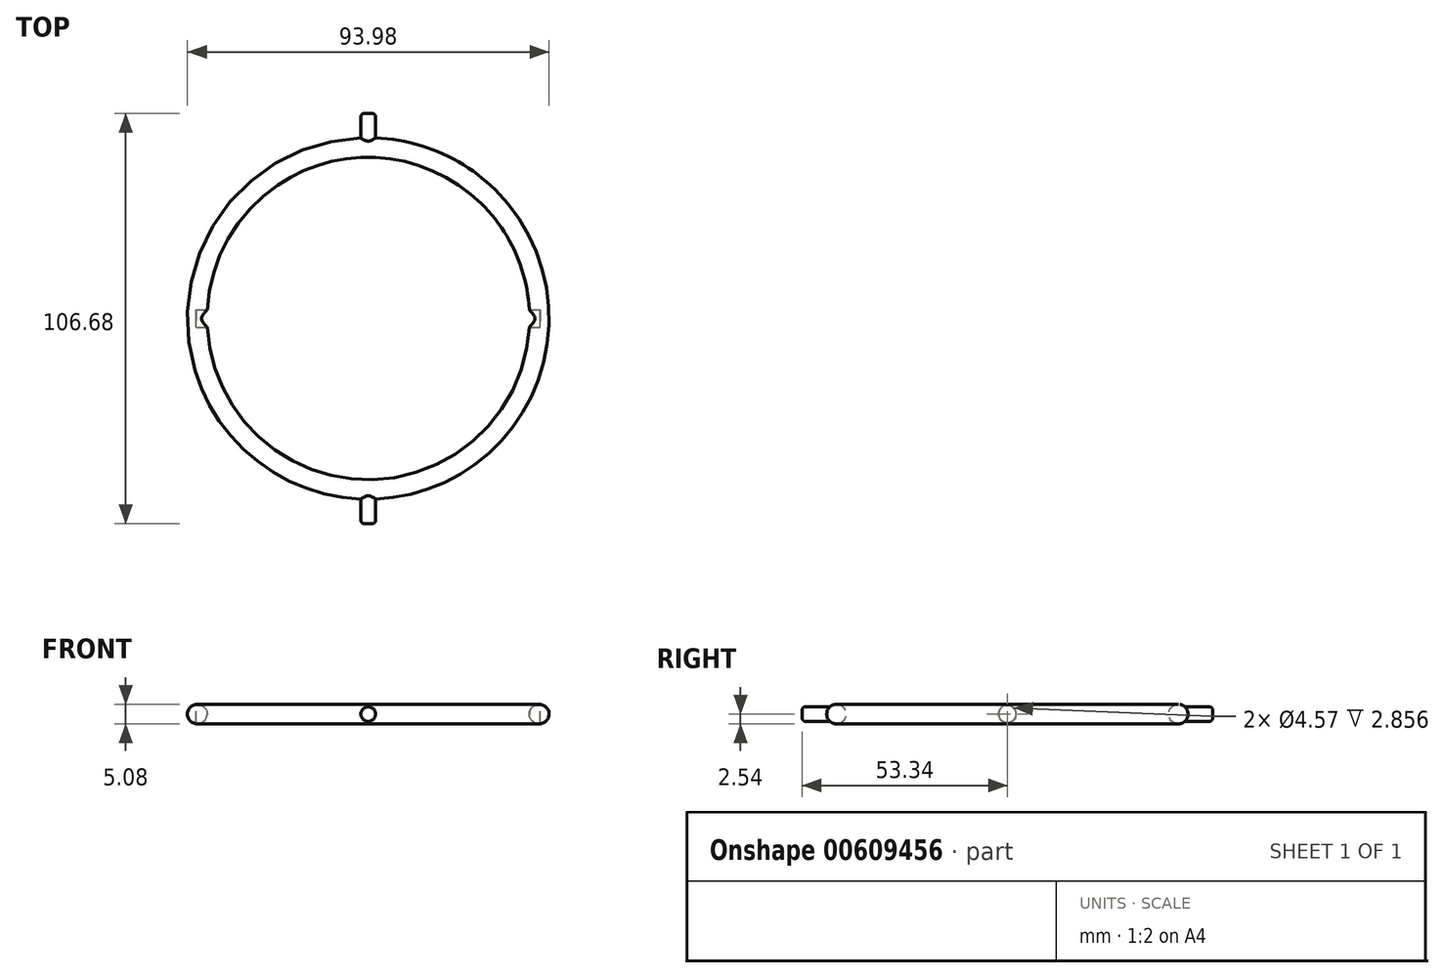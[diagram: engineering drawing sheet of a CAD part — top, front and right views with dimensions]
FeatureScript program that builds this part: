
annotation { "Feature Type Name" : "Feature", "Feature Type Description" : "" }
export const myFeature = defineFeature(function(context is Context, id is Id, definition is map)
    precondition{}
    {
        {
            var Q0;
            Q0=qCreatedBy(makeId("Top.planeOp"),FACE);
            var sketch = newSketch(context, id + "F0", { "sketchPlane" : qUnion([Q0])});
            skCircle(sketch, "E0", {"center": v(0, 0) * mm, "radius": 44.45 * mm});
            skSolve(sketch);
        }
        {
            var Q0;
            Q0=qCreatedBy(makeId("Right.planeOp"),FACE);
            var sketch = newSketch(context, id + "F1", { "sketchPlane" : qUnion([Q0])});
            skCircle(sketch, "E1", {"center": v(-44.45, 0) * mm, "radius": 2.54 * mm});
            skSolve(sketch);
        }
        {
            var Q0;
            Q0=makeQuery(id+"F1.imprint","IMPRINT",FACE,{"disambiguationData":[TD([[makeQuery(id+"F1.imprint","IMPRINT",EDGE,{"derivedFrom":sQuery(id+"F1.wireOp",EDGE,"E1")}),1.0]])]});
            var Q1;
            Q1=sQuery(id+"F0.wireOp",EDGE,"E0");
            sweep(context, id + "F2", {"profiles" : qUnion([Q0]), "path" : qUnion([Q1])});
        }
        {
            var Q0;
            Q0=qCreatedBy(makeId("Front.planeOp"),FACE);
            cPlane(context, id + "F3", {"entities" : qUnion([Q0]), "cplaneType" : CPlaneType.OFFSET, "offset" : 53.34 * mm, "width" : 152.4 * mm, "height" : 152.4 * mm});
        }
        {
            var Q0;
            Q0=qCreatedBy(id+"F3.planeOp",FACE);
            var sketch = newSketch(context, id + "F4", { "sketchPlane" : qUnion([Q0])});
            skCircle(sketch, "E2", {"center": v(0, 0) * mm, "radius": 1.9 * mm});
            skSolve(sketch);
        }
        {
            var Q0;
            Q0=makeQuery(id+"F4.imprint","IMPRINT",FACE,{"disambiguationData":[TD([[makeQuery(id+"F4.imprint","IMPRINT",EDGE,{"derivedFrom":sQuery(id+"F4.wireOp",EDGE,"E2")}),1.0]])]});
            extrude(context, id + "F5", {"entities" : qUnion([Q0]), "operationType" : NewBodyOperationType.ADD, "endBound" : BoundingType.UP_TO_NEXT, "oppositeDirection" : true, "depth" : 25.4 * mm, "offsetDistance" : 25.4 * mm});
        }
        {
            var Q0;
            Q0=makeQuery(id+"F5.opExtrude","CAP_FACE",FACE,{"disambiguationData":[OSD([sQuery(id+"F4.wireOp",EDGE,"E2")])],"isStart":true});
            fillet(context, id + "F6", {"entities" : qUnion([Q0]), "radius" : 0.89 * mm, "tangentPropagation" : true, "allowEdgeOverflow" : false});
        }
        {
            var Q0;
            Q0=makeQuery(id+"F2.opSweep","SWEPT_BODY",BODY,{"disambiguationData":[OSD([sQuery(id+"F0.wireOp",EDGE,"E0"),sQuery(id+"F1.wireOp",EDGE,"E1")])]});
            var Q1;
            Q1=qCreatedBy(makeId("Front.planeOp"),FACE);
            mirror(context, id + "F7", {"operationType" : NewBodyOperationType.ADD, "entities" : qUnion([Q0]), "mirrorPlane" : qUnion([Q1])});
        }
        {
            var Q0;
            Q0=qCreatedBy(makeId("Right.planeOp"),FACE);
            var sketch = newSketch(context, id + "F8", { "sketchPlane" : qUnion([Q0])});
            skCircle(sketch, "E3", {"center": v(0, 0) * mm, "radius": 2.29 * mm});
            skSolve(sketch);
        }
        {
            var Q0;
            Q0=makeQuery(id+"F8.imprint","IMPRINT",FACE,{"disambiguationData":[TD([[makeQuery(id+"F8.imprint","IMPRINT",EDGE,{"derivedFrom":sQuery(id+"F8.wireOp",EDGE,"E3")}),1.0]])]});
            extrude(context, id + "F9", {"entities" : qUnion([Q0]), "operationType" : NewBodyOperationType.REMOVE, "oppositeDirection" : true, "depth" : 44.7 * mm, "offsetDistance" : 25.4 * mm, "hasSecondDirection" : true, "secondDirectionOppositeDirection" : false, "secondDirectionDepth" : 44.7 * mm});
        }
    });
